# Revit family: Inkoo Pro sofa
name_source: partatom
category: Furniture
revit_build: Autodesk Revit 2015 (Build: 20140606_1530(x64)
units: mm (PartAtom-declared; Revit-internal decimal feet)

## types (4) — shared parameters
1st cushion = Yes
Back support cushion type = Inkoo cushion : Cushion 650x500x145 back support
Cushion location = 100 mm  [stored 0.328084 ft]
Manufacturer = Isku Oy
Seat cushion type = Inkoo cushion : Cushion 650x700x145 seat
Type Comments = Available as antimicrobial
URL = www.isku.fi

## per-type parameters (varying)
| type | 2nd cushion | 3rd cushion | Left Arm Visibility | Material legs | Platform | Right Arm Visibility | Seat support | Sofa Width |
| Inkoo pro 3 persons with armrest | Yes | Yes | Yes | RAL 9006 Abloy Aluminum grey | Inkoo cushion : Support platform 900x2150x20 | Yes | Inkoo cushion : Seat 2150 | 2150 mm |
| Inkoo pro 2 persons with armrest | Yes | No | Yes | Aluminum | Inkoo cushion : Support platform 900x1500x20 | Yes | Inkoo cushion : Seat 1500 | 1500 mm  [stored 4.92126 ft] |
| Inkoo pro 1 persons with armrest | No | No | Yes | Aluminum | Inkoo cushion : Support platform 900x850x20 | Yes | Inkoo cushion : Seat 850 | 850 mm  [stored 2.78871 ft] |
| Inkoo pro 1 persons no armrest | No | No | No | Aluminum | Inkoo cushion : Support platform 900x650x20 | No | Inkoo cushion : Seat 650 | 850 mm  [stored 2.78871 ft] |

note: [stored X ft] marks values corroborated as IEEE doubles in the binary element streams (Revit-internal decimal feet)

## geometry (parser evidence)
native form markers: Blend x4, Sweep x6
no freeform markers — native parametric forms only
